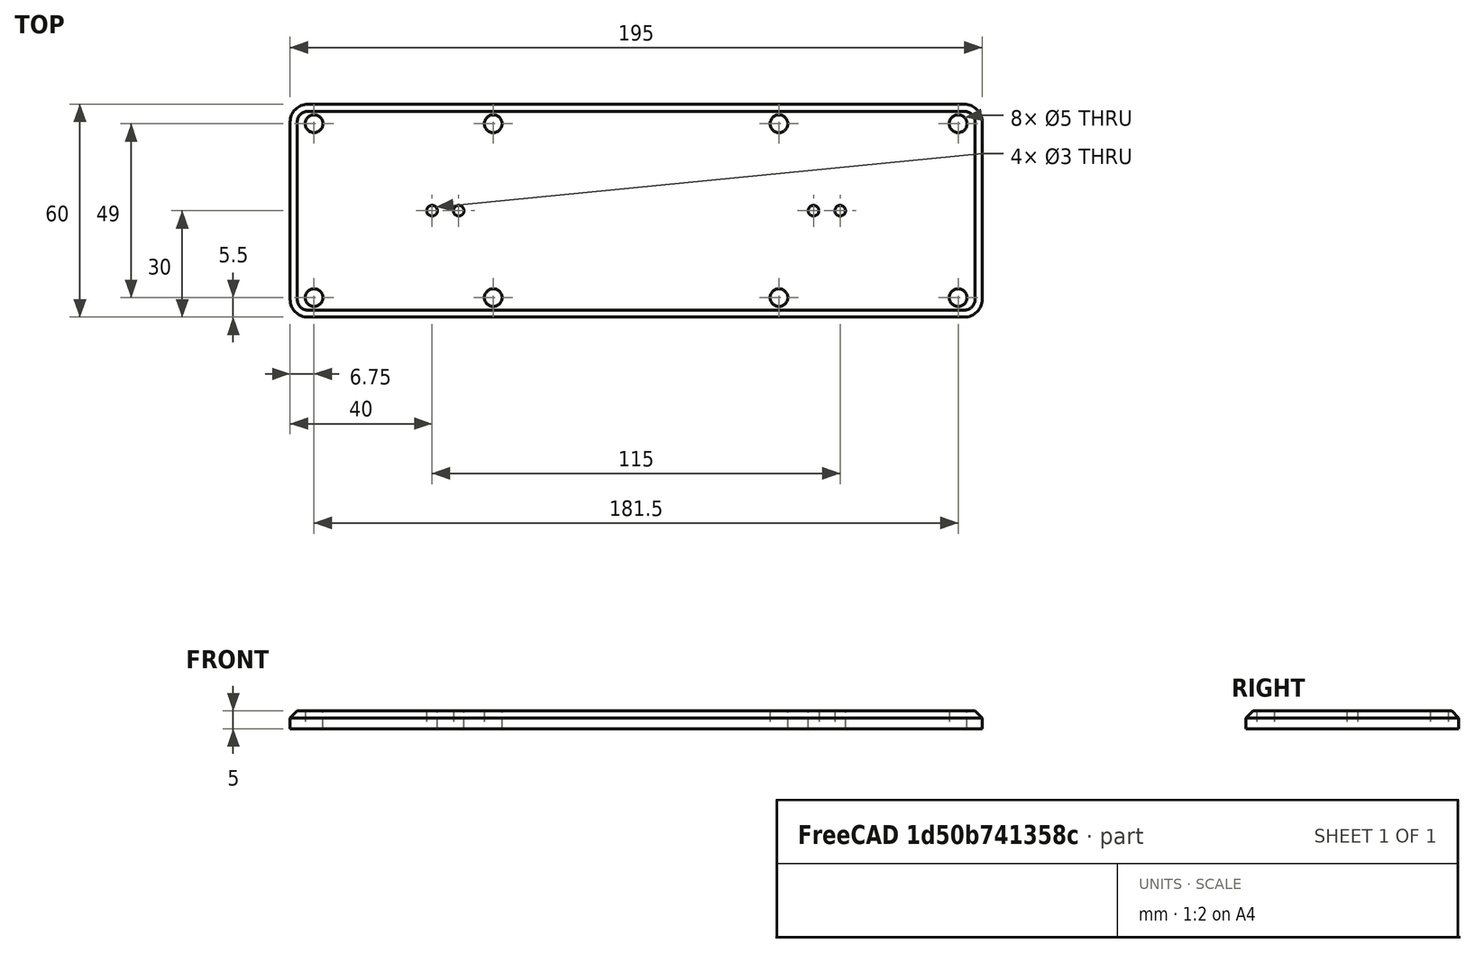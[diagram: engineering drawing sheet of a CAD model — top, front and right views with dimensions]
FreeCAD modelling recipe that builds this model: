
FCSTD DOCUMENT  (FreeCAD 0.20R29410 (Git))
Label: mounting plate
License: All rights reserved
LicenseURL: http://en.wikipedia.org/wiki/All_rights_reserved
objects: Sketcher::SketchObject×3, PartDesign::Pocket×2, Mesh::Feature×2, PartDesign::Pad×1, PartDesign::Fillet×1, PartDesign::Chamfer×1, PartDesign::Mirrored×1, PartDesign::MultiTransform×1, PartDesign::Body×1, App::Part×1
note: 16 computed .brp shape members not serialized (recipe doc carries the construction recipe); baked Part::Feature solids carry a one-line shape summary decoded from their .brp

FEATURE [Sketcher::SketchObject] Sketch
  FullyConstrained = true
  MapMode = 5
  Support = -> [XY_Plane001]
  sketch-geometry (1):
    g0: Circle CenterX=-50 CenterY=0 CenterZ=0 NormalX=0 NormalY=0 NormalZ=1 AngleXU=0 Radius=1.5
  constraints (3):
    c: PointOnObject(g0,g-1)
    c: Diameter(g0) = 3
    c: DistanceX(g0,g-1) = 50
FEATURE [Sketcher::SketchObject] Sketch001
  FullyConstrained = true
  MapMode = 5
  Support = -> [XY_Plane001]
  sketch-geometry (20):
    g0: LineSegment StartX=97.5 StartY=-30 StartZ=0 EndX=-97.5 EndY=-30 EndZ=0
    g1: LineSegment StartX=-97.5 StartY=-30 StartZ=0 EndX=-97.5 EndY=30 EndZ=0
    g2: LineSegment StartX=-97.5 StartY=30 StartZ=0 EndX=97.5 EndY=30 EndZ=0
    g3: LineSegment StartX=97.5 StartY=30 StartZ=0 EndX=97.5 EndY=-30 EndZ=0
    g4: LineSegment StartX=-40.25 StartY=24.5 StartZ=0 EndX=-90.75 EndY=24.5 EndZ=0
    g5: LineSegment StartX=-90.75 StartY=24.5 StartZ=0 EndX=-90.75 EndY=-24.5 EndZ=0
    g6: LineSegment StartX=-90.75 StartY=-24.5 StartZ=0 EndX=-40.25 EndY=-24.5 EndZ=0
    g7: LineSegment StartX=-40.25 StartY=-24.5 StartZ=0 EndX=-40.25 EndY=24.5 EndZ=0
    g8: Circle CenterX=-40.25 CenterY=24.5 CenterZ=0 NormalX=0 NormalY=0 NormalZ=1 AngleXU=0 Radius=2.5
    g9: Circle CenterX=-90.75 CenterY=24.5 CenterZ=0 NormalX=0 NormalY=0 NormalZ=1 AngleXU=0 Radius=2.5
    g10: Circle CenterX=-90.75 CenterY=-24.5 CenterZ=0 NormalX=0 NormalY=0 NormalZ=1 AngleXU=0 Radius=2.5
    g11: Circle CenterX=-40.25 CenterY=-24.5 CenterZ=0 NormalX=0 NormalY=0 NormalZ=1 AngleXU=0 Radius=2.5
    g12: LineSegment StartX=40.25 StartY=24.5 StartZ=0 EndX=90.75 EndY=24.5 EndZ=0
    g13: LineSegment StartX=90.75 StartY=24.5 StartZ=0 EndX=90.75 EndY=-24.5 EndZ=0
    g14: LineSegment StartX=90.75 StartY=-24.5 StartZ=0 EndX=40.25 EndY=-24.5 EndZ=0
    g15: LineSegment StartX=40.25 StartY=-24.5 StartZ=0 EndX=40.25 EndY=24.5 EndZ=0
    g16: Circle CenterX=40.25 CenterY=24.5 CenterZ=0 NormalX=0 NormalY=0 NormalZ=1 AngleXU=0 Radius=2.5
    g17: Circle CenterX=90.75 CenterY=24.5 CenterZ=0 NormalX=0 NormalY=0 NormalZ=1 AngleXU=0 Radius=2.5
    g18: Circle CenterX=90.75 CenterY=-24.5 CenterZ=0 NormalX=0 NormalY=0 NormalZ=1 AngleXU=0 Radius=2.5
    g19: Circle CenterX=40.25 CenterY=-24.5 CenterZ=0 NormalX=0 NormalY=0 NormalZ=1 AngleXU=0 Radius=2.5
  constraints (50):
    c: Coincident(g0,g1)
    c: Coincident(g1,g2)
    c: Coincident(g2,g3)
    c: Coincident(g3,g0)
    c: Horizontal(g0)
    c: Horizontal(g2)
    c: Vertical(g1)
    c: Vertical(g3)
    c: Symmetric(g0,g1,g-1)
    c: DistanceX(g2,g2) = 195
    c: DistanceY(g1,g1) = 60
    c: Coincident(g4,g5)
    c: Coincident(g5,g6)
    c: Coincident(g6,g7)
    c: Coincident(g7,g4)
    c: Horizontal(g4)
    c: Horizontal(g6)
    c: Vertical(g5)
    c: Vertical(g7)
    c: DistanceY(g5,g5) = 49
    c: DistanceX(g4,g4) = 50.5
    c: DistanceY(g-1,g4) = 24.5
    c: Coincident(g8,g4)
    c: Coincident(g9,g4)
    c: Coincident(g10,g5)
    c: Coincident(g11,g6)
    c: Diameter(g8) = 5
    c: Diameter(g9) = 5
    c: Diameter(g10) = 5
    c: Diameter(g11) = 5
    c: Coincident(g12,g13)
    c: Coincident(g13,g14)
    c: Coincident(g14,g15)
    c: Coincident(g15,g12)
    c: Horizontal(g12)
    c: Horizontal(g14)
    c: Vertical(g13)
    c: Vertical(g15)
    c: DistanceX(g12,g12) = 50.5
    c: DistanceY(g13,g13) = 49
    c: Coincident(g16,g12)
    c: Coincident(g17,g12)
    c: Coincident(g18,g13)
    c: Coincident(g19,g14)
    c: Diameter(g16) = 5
    c: Diameter(g19) = 5
    c: Diameter(g17) = 5
    c: Diameter(g18) = 5
    c: Distance(g8,g16) = 80.5
    c: Symmetric(g8,g16,g-2)
FEATURE [PartDesign::Pad] Pad
  Direction = (0,0,1)
  Length = 5
  Length2 = 10
  Profile = -> Sketch001
  ReferenceAxis = -> Sketch001 [N_Axis]
  Type = 0
FEATURE [PartDesign::Fillet] Fillet
  Base = -> Pad [Edge2,Edge1,Edge8,Edge5]
  BaseFeature = -> Pad
  Radius = 5
  SupportTransform = false
  UseAllEdges = false
FEATURE [PartDesign::Chamfer] Chamfer
  Angle = 45
  Base = -> Fillet [Edge4]
  BaseFeature = -> Fillet
  ChamferType = 0
  FlipDirection = false
  Size = 2
  Size2 = 1
  SupportTransform = false
  UseAllEdges = false
FEATURE [PartDesign::Pocket] Pocket
  BaseFeature = -> Chamfer
  Direction = (0,0,-1)
  Length = 5
  Length2 = 5
  Profile = -> Sketch
  ReferenceAxis = -> Sketch [N_Axis]
  Reversed = true
  Type = 1
FEATURE [PartDesign::Mirrored] Mirrored
  MirrorPlane = -> Sketch [V_Axis]
FEATURE [PartDesign::MultiTransform] MultiTransform
  BaseFeature = -> Pocket
  Originals = -> [Pocket]
  Transformations = -> [Mirrored]
FEATURE [Mesh::Feature] Handle_MEDIUM
  Placement = pos=(-60,9,5) rot=(1,0,0;1.5708rad)
FEATURE [Sketcher::SketchObject] Sketch002
  FullyConstrained = true
  MapMode = 5
  Support = -> [XY_Plane001]
  sketch-geometry (2):
    g0: Circle CenterX=57.5 CenterY=0 CenterZ=0 NormalX=0 NormalY=0 NormalZ=1 AngleXU=0 Radius=1.5
    g1: Circle CenterX=-57.5 CenterY=0 CenterZ=0 NormalX=0 NormalY=0 NormalZ=1 AngleXU=0 Radius=1.5
  constraints (6):
    c: PointOnObject(g0,g-1)
    c: PointOnObject(g1,g-1)
    c: Diameter(g1) = 3
    c: Diameter(g0) = 3
    c: DistanceX(g1,g0) = 115
    c: DistanceX(g1,g-1) = 57.5
FEATURE [PartDesign::Pocket] Pocket001
  BaseFeature = -> MultiTransform
  Direction = (0,0,-1)
  Length = 5
  Length2 = 5
  Profile = -> Sketch002
  ReferenceAxis = -> Sketch002 [N_Axis]
  Reversed = true
  Type = 1
FEATURE [PartDesign::Body] Body
  Group = -> [Sketch001,Pad,Fillet,Chamfer,Sketch,Pocket,MultiTransform,Mirrored,Sketch002,Pocket001]
  Origin = -> Origin001
  Tip = -> Pocket001
FEATURE [App::Part] Part
  Group = -> [Body]
  Origin = -> Origin
FEATURE [Mesh::Feature] Handle_LARGE
  Placement = pos=(-69,10.5403,4.29581) rot=(1,0,0;1.5708rad)
